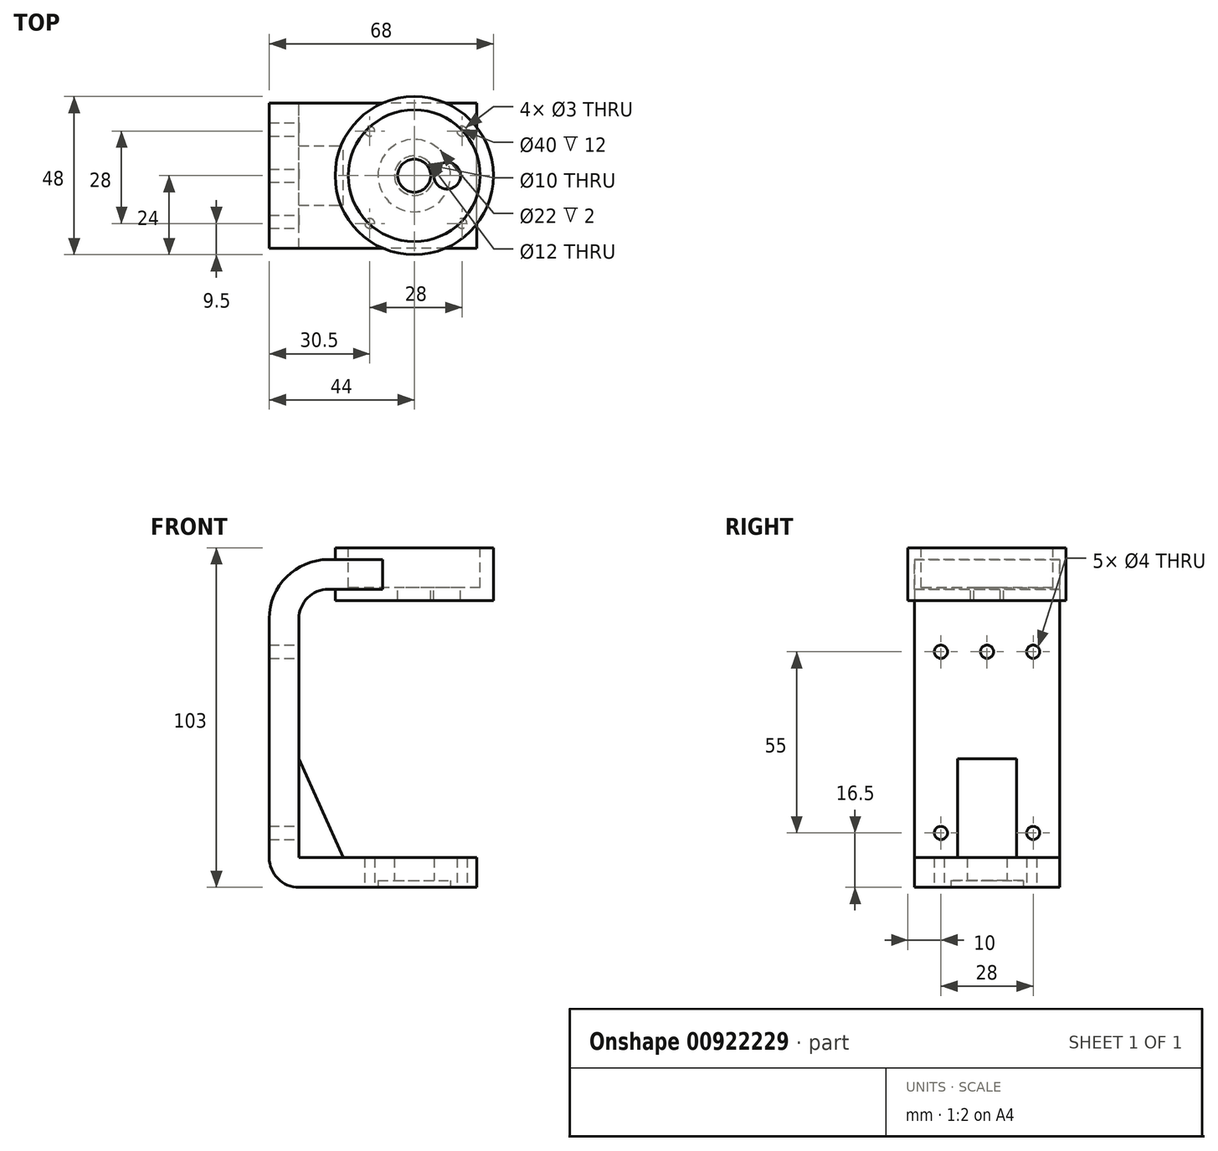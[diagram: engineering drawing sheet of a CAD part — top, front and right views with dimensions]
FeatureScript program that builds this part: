
annotation { "Feature Type Name" : "Feature", "Feature Type Description" : "" }
export const myFeature = defineFeature(function(context is Context, id is Id, definition is map)
    precondition{}
    {
        {
            var Q0;
            Q0=qCreatedBy(makeId("Front.planeOp"),FACE);
            var sketch = newSketch(context, id + "F0", { "sketchPlane" : qUnion([Q0])});
            skLineSegment(sketch, "E0.bottom", {"start": v(-14, 64) * mm, "end": v(34, 64) * mm});
            skLineSegment(sketch, "E0.top", {"start": v(-14, 48) * mm, "end": v(34, 48) * mm});
            skLineSegment(sketch, "E0.left", {"start": v(-14, 64) * mm, "end": v(-14, 48) * mm});
            skLineSegment(sketch, "E0.right", {"start": v(34, 64) * mm, "end": v(34, 48) * mm});
            skLineSegment(sketch, "E1", {"start": v(-25, 42.5) * mm, "end": v(-25, -30) * mm});
            skLineSegment(sketch, "E2", {"start": v(-25, -30) * mm, "end": v(29, -30) * mm});
            skLineSegment(sketch, "E3", {"start": v(29, -30) * mm, "end": v(29, -39) * mm});
            skLineSegment(sketch, "E4", {"start": v(29, -39) * mm, "end": v(-25, -39) * mm});
            skArc(sketch, "E5", {"start": v(-16, 51.5) * mm, "mid": v(-22.36, 48.86) * mm, "end": v(-25, 42.5) * mm});
            skLineSegment(sketch, "E6", {"start": v(-16, 51.5) * mm, "end": v(10, 51.5) * mm});
            skLineSegment(sketch, "E7.0", {"start": v(-16, 60.5) * mm, "end": v(10, 60.5) * mm});
            skArc(sketch, "E7.1", {"start": v(-16, 60.5) * mm, "mid": v(-28.73, 55.23) * mm, "end": v(-34, 42.5) * mm});
            skLineSegment(sketch, "E8.0", {"start": v(-34, 42.5) * mm, "end": v(-34, -30) * mm});
            skArc(sketch, "E9", {"start": v(-34, -30) * mm, "mid": v(-31.36, -36.36) * mm, "end": v(-25, -39) * mm});
            skLineSegment(sketch, "E10", {"start": v(-25, -30) * mm, "end": v(-25, -39) * mm});
            skLineSegment(sketch, "E11", {"start": v(10, 60.5) * mm, "end": v(10, 51.5) * mm});
            skLineSegment(sketch, "E12", {"start": v(10, 64) * mm, "end": v(10, 48) * mm});
            skLineSegment(sketch, "E13", {"start": v(-16, 51.5) * mm, "end": v(-16, 60.5) * mm});
            skLineSegment(sketch, "E14", {"start": v(10, 68.5) * mm, "end": v(10, 42.48) * mm, "construction": true});
            skPoint(sketch, "E15.oppositeSnap0", {"position": v(2, -30) * mm});
            skLineSegment(sketch, "E15.bottom", {"start": v(-25, -30) * mm, "end": v(2, -30) * mm, "construction": true});
            skLineSegment(sketch, "E15.top", {"start": v(-25, 0) * mm, "end": v(2, 0) * mm, "construction": true});
            skLineSegment(sketch, "E15.left", {"start": v(-25, -30) * mm, "end": v(-25, 0) * mm, "construction": true});
            skLineSegment(sketch, "E15.right", {"start": v(2, -30) * mm, "end": v(2, 0) * mm, "construction": true});
            skLineSegment(sketch, "E16", {"start": v(-11.5, -30) * mm, "end": v(-25, 0) * mm});
            skSolve(sketch);
        }
        {
            var Q0;
            Q0=makeQuery(id+"F0.imprint","IMPRINT",FACE,{"disambiguationData":[TD([[makeQuery(id+"F0.imprint","IMPRINT",EDGE,{"derivedFrom":sQuery(id+"F0.wireOp",EDGE,"E1")}),-1.0]])]});
            var Q1;
            Q1=makeQuery(id+"F0.imprint","IMPRINT",FACE,{"disambiguationData":[TD([[makeQuery(id+"F0.imprint","IMPRINT",EDGE,{"derivedFrom":sQuery(id+"F0.wireOp",EDGE,"E6")}),1.0]])]});
            var Q2;
            Q2=makeQuery(id+"F0.imprint","IMPRINT",FACE,{"disambiguationData":[TD([[makeQuery(id+"F0.imprint","IMPRINT",EDGE,{"derivedFrom":sQuery(id+"F0.wireOp",EDGE,"E2")}),-1.0]])]});
            extrude(context, id + "F1", {"entities" : qUnion([Q0, Q1, Q2]), "endBound" : BoundingType.SYMMETRIC, "depth" : 44 * mm, "offsetDistance" : 25 * mm});
        }
        {
            var Q0;
            {var subQ0=sQuery(id+"F0.wireOp",EDGE,"E0.right");Q0=makeQuery(id+"F0.imprint","IMPRINT",FACE,{"disambiguationData":[TD([[makeQuery(id+"F0.imprint","IMPRINT",EDGE,{"derivedFrom":subQ0}),-1.0]])]});}
            var Q1;
            Q1=sQuery(id+"F0.wireOp",EDGE,"E14");
            revolve(context, id + "F2", {"operationType" : NewBodyOperationType.ADD, "surfaceOperationType" : NewSurfaceOperationType.NEW, "entities" : qUnion([Q0]), "axis" : qUnion([Q1]), "revolveType" : RevolveType.FULL});
        }
        {
            var Q0;
            Q0=makeQuery(id+"F2.opRevolve","SWEPT_FACE",FACE,{"disambiguationData":[OSD([sQuery(id+"F0.wireOp",EDGE,"E0.bottom")])]});
            var sketch = newSketch(context, id + "F3", { "sketchPlane" : qUnion([Q0])});
            skCircle(sketch, "E17", {"center": v(10, 0) * mm, "radius": 20 * mm});
            skSolve(sketch);
        }
        {
            var Q0;
            Q0=qSketchRegion(id+"F3",true);
            extrude(context, id + "F4", {"entities" : qUnion([Q0]), "operationType" : NewBodyOperationType.REMOVE, "oppositeDirection" : true, "depth" : 12 * mm, "offsetDistance" : 25 * mm});
        }
        {
            var Q0;
            Q0=makeQuery(id+"F4.boolean.opBoolean","COPY",FACE,{"derivedFrom":makeQuery(id+"F4.opExtrude","CAP_FACE",FACE,{"disambiguationData":[OSD([sQuery(id+"F3.wireOp",EDGE,"E17")])],"isStart":false})});
            var sketch = newSketch(context, id + "F5", { "sketchPlane" : qUnion([Q0])});
            skCircle(sketch, "E18", {"center": v(10, 0) * mm, "radius": 5 * mm});
            skCircle(sketch, "E19", {"center": v(20, 0) * mm, "radius": 4.05 * mm});
            skSolve(sketch);
        }
        {
            var Q0;
            Q0=makeQuery(id+"F5.imprint","IMPRINT",FACE,{"disambiguationData":[TD([[makeQuery(id+"F5.imprint","IMPRINT",EDGE,{"derivedFrom":sQuery(id+"F5.wireOp",EDGE,"E18")}),1.0]])]});
            var Q1;
            Q1=makeQuery(id+"F5.imprint","IMPRINT",FACE,{"disambiguationData":[TD([[makeQuery(id+"F5.imprint","IMPRINT",EDGE,{"derivedFrom":sQuery(id+"F5.wireOp",EDGE,"E19")}),1.0]])]});
            extrude(context, id + "F6", {"entities" : qUnion([Q0, Q1]), "operationType" : NewBodyOperationType.REMOVE, "oppositeDirection" : true, "depth" : 50 * mm, "offsetDistance" : 25 * mm});
        }
        {
            var Q0;
            Q0=makeQuery(id+"F1.opExtrude","SWEPT_FACE",FACE,{"disambiguationData":[OSD([sQuery(id+"F0.wireOp",EDGE,"E1")])]});
            var sketch = newSketch(context, id + "F7", { "sketchPlane" : qUnion([Q0])});
            skCircle(sketch, "E20", {"center": v(14, -22.5) * mm, "radius": 2 * mm});
            skLineSegment(sketch, "E21", {"start": v(17.15, 0) * mm, "end": v(-19.12, 0) * mm, "construction": true});
            skCircle(sketch, "E22.0.1.0", {"center": v(14, 32.5) * mm, "radius": 2 * mm});
            skCircle(sketch, "E22.1.0.0", {"center": v(0, -22.5) * mm, "radius": 2 * mm});
            skCircle(sketch, "E22.1.1.0", {"center": v(0, 32.5) * mm, "radius": 2 * mm});
            skCircle(sketch, "E22.2.0.0", {"center": v(-14, -22.5) * mm, "radius": 2 * mm});
            skCircle(sketch, "E22.2.1.0", {"center": v(-14, 32.5) * mm, "radius": 2 * mm});
            skLineSegment(sketch, "E22.direction1", {"start": v(14, -22.5) * mm, "end": v(0, -22.5) * mm, "construction": true});
            skLineSegment(sketch, "E22.direction2", {"start": v(14, -22.5) * mm, "end": v(14, 32.5) * mm, "construction": true});
            skSolve(sketch);
        }
        {
            var Q0;
            Q0=makeQuery(id+"F7.imprint","IMPRINT",FACE,{"disambiguationData":[TD([[makeQuery(id+"F7.imprint","IMPRINT",EDGE,{"derivedFrom":sQuery(id+"F7.wireOp",EDGE,"E20")}),1.0]])]});
            var Q1;
            Q1=makeQuery(id+"F7.imprint","IMPRINT",FACE,{"disambiguationData":[TD([[makeQuery(id+"F7.imprint","IMPRINT",EDGE,{"derivedFrom":sQuery(id+"F7.wireOp",EDGE,"E22.0.1.0")}),1.0]])]});
            var Q2;
            Q2=makeQuery(id+"F7.imprint","IMPRINT",FACE,{"disambiguationData":[TD([[makeQuery(id+"F7.imprint","IMPRINT",EDGE,{"derivedFrom":sQuery(id+"F7.wireOp",EDGE,"E22.1.1.0")}),1.0]])]});
            var Q3;
            Q3=makeQuery(id+"F7.imprint","IMPRINT",FACE,{"disambiguationData":[TD([[makeQuery(id+"F7.imprint","IMPRINT",EDGE,{"derivedFrom":sQuery(id+"F7.wireOp",EDGE,"E22.2.0.0")}),1.0]])]});
            var Q4;
            Q4=makeQuery(id+"F7.imprint","IMPRINT",FACE,{"disambiguationData":[TD([[makeQuery(id+"F7.imprint","IMPRINT",EDGE,{"derivedFrom":sQuery(id+"F7.wireOp",EDGE,"E22.2.1.0")}),1.0]])]});
            extrude(context, id + "F8", {"entities" : qUnion([Q0, Q1, Q2, Q3, Q4]), "operationType" : NewBodyOperationType.REMOVE, "endBound" : BoundingType.THROUGH_ALL, "oppositeDirection" : true, "depth" : 25 * mm, "offsetDistance" : 25 * mm});
        }
        {
            var Q0;
            Q0=makeQuery(id+"F1.opExtrude","SWEPT_FACE",FACE,{"disambiguationData":[OSD([sQuery(id+"F0.wireOp",EDGE,"E4")])]});
            var sketch = newSketch(context, id + "F9", { "sketchPlane" : qUnion([Q0])});
            skCircle(sketch, "E23", {"center": v(10, 0) * mm, "radius": 11 * mm});
            skSolve(sketch);
        }
        {
            var Q0;
            Q0=qSketchRegion(id+"F9",true);
            extrude(context, id + "F10", {"entities" : qUnion([Q0]), "operationType" : NewBodyOperationType.REMOVE, "oppositeDirection" : true, "depth" : 2 * mm, "offsetDistance" : 25 * mm});
        }
        {
            var Q0;
            Q0=makeQuery(id+"F1.opExtrude","SWEPT_FACE",FACE,{"disambiguationData":[OSD([sQuery(id+"F0.wireOp",EDGE,"E4")])]});
            var sketch = newSketch(context, id + "F11", { "sketchPlane" : qUnion([Q0])});
            skCircle(sketch, "E24", {"center": v(-3.5, -13.5) * mm, "radius": 1.5 * mm});
            skCircle(sketch, "E25.0.1.0", {"center": v(-3.5, 14.5) * mm, "radius": 1.5 * mm});
            skCircle(sketch, "E25.1.0.0", {"center": v(24.5, -13.5) * mm, "radius": 1.5 * mm});
            skCircle(sketch, "E25.1.1.0", {"center": v(24.5, 14.5) * mm, "radius": 1.5 * mm});
            skCircle(sketch, "E25.2.0.0", {"center": v(52.5, -13.5) * mm, "radius": 1.5 * mm});
            skCircle(sketch, "E25.2.1.0", {"center": v(52.5, 14.5) * mm, "radius": 1.5 * mm});
            skLineSegment(sketch, "E25.direction1", {"start": v(-3.5, -13.5) * mm, "end": v(24.5, -13.5) * mm, "construction": true});
            skLineSegment(sketch, "E25.direction2", {"start": v(-3.5, -13.5) * mm, "end": v(-3.5, 14.5) * mm, "construction": true});
            skSolve(sketch);
        }
        {
            var Q0;
            Q0=qSketchRegion(id+"F11",true);
            extrude(context, id + "F12", {"entities" : qUnion([Q0]), "operationType" : NewBodyOperationType.REMOVE, "oppositeDirection" : true, "depth" : 20 * mm, "offsetDistance" : 25 * mm});
        }
        {
            var Q0;
            Q0=makeQuery(id+"F1.opExtrude","SWEPT_FACE",FACE,{"disambiguationData":[OSD([sQuery(id+"F0.wireOp",EDGE,"E4")])]});
            var sketch = newSketch(context, id + "F13", { "sketchPlane" : qUnion([Q0])});
            skCircle(sketch, "E26", {"center": v(10, 0) * mm, "radius": 6 * mm});
            skSolve(sketch);
        }
        {
            var Q0;
            Q0=makeQuery(id+"F13.imprint","IMPRINT",FACE,{"disambiguationData":[TD([[makeQuery(id+"F13.imprint","IMPRINT",EDGE,{"derivedFrom":sQuery(id+"F13.wireOp",EDGE,"E26")}),1.0]])]});
            extrude(context, id + "F14", {"entities" : qUnion([Q0]), "operationType" : NewBodyOperationType.REMOVE, "oppositeDirection" : true, "depth" : 25 * mm, "offsetDistance" : 25 * mm});
        }
        {
            var Q0;
            {var subQ3=sQuery(id+"F0.wireOp",EDGE,"E16");Q0=makeQuery(id+"F0.imprint","IMPRINT",FACE,{"disambiguationData":[TD([[makeQuery(id+"F0.imprint","IMPRINT",EDGE,{"derivedFrom":subQ3}),1.0]])]});}
            extrude(context, id + "F15", {"entities" : qUnion([Q0]), "operationType" : NewBodyOperationType.ADD, "endBound" : BoundingType.SYMMETRIC, "depth" : 18 * mm, "offsetDistance" : 25 * mm});
        }
    });
